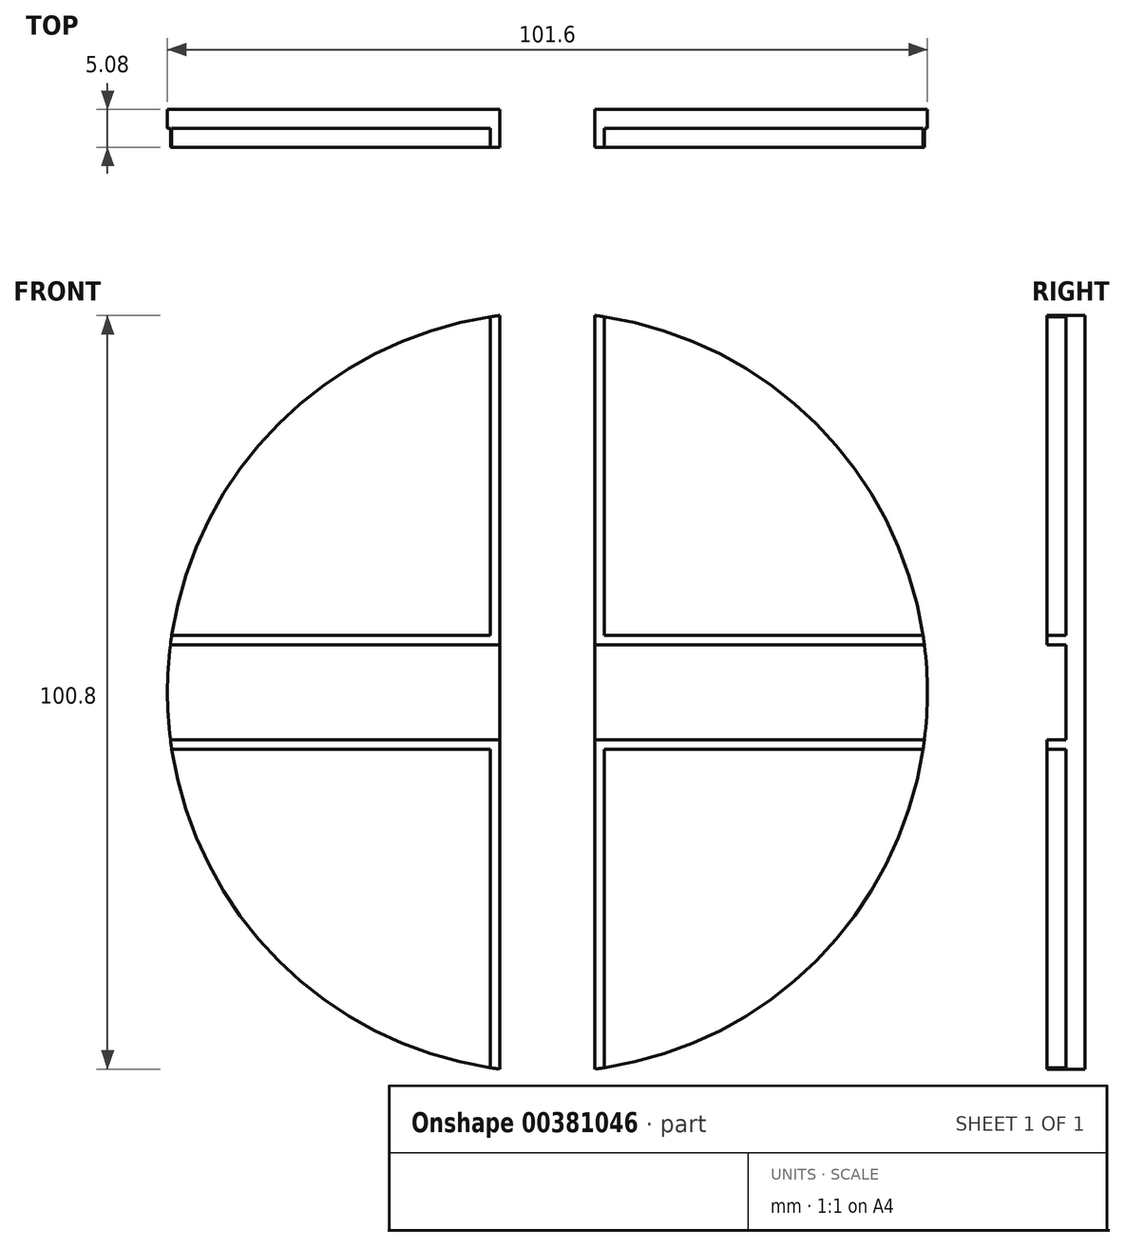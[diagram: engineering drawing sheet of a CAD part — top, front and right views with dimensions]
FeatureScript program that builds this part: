
annotation { "Feature Type Name" : "Feature", "Feature Type Description" : "" }
export const myFeature = defineFeature(function(context is Context, id is Id, definition is map)
    precondition{}
    {
        {
            var Q0;
            Q0=qCreatedBy(makeId("Front.planeOp"),FACE);
            var sketch = newSketch(context, id + "F0", { "sketchPlane" : qUnion([Q0])});
            skCircle(sketch, "E0", {"center": v(0, 0) * mm, "radius": 50.8 * mm});
            skLineSegment(sketch, "E1.bottom", {"start": v(6.35, 6.35) * mm, "end": v(-6.35, 6.35) * mm});
            skLineSegment(sketch, "E1.top", {"start": v(6.35, -6.35) * mm, "end": v(-6.35, -6.35) * mm});
            skLineSegment(sketch, "E1.left", {"start": v(6.35, 6.35) * mm, "end": v(6.35, -6.35) * mm});
            skLineSegment(sketch, "E1.right", {"start": v(-6.35, 6.35) * mm, "end": v(-6.35, -6.35) * mm});
            skLineSegment(sketch, "E2", {"start": v(-6.35, -50.4) * mm, "end": v(-6.35, 50.4) * mm});
            skLineSegment(sketch, "E3", {"start": v(6.35, 50.4) * mm, "end": v(6.35, -50.4) * mm});
            skLineSegment(sketch, "E4", {"start": v(50.4, -6.35) * mm, "end": v(-50.4, -6.35) * mm});
            skPoint(sketch, "E4.startSnap0", {"position": v(0, -6.35) * mm});
            skLineSegment(sketch, "E5", {"start": v(-50.4, 6.35) * mm, "end": v(50.4, 6.35) * mm});
            skPoint(sketch, "E5.startSnap0", {"position": v(0, 6.35) * mm});
            skLineSegment(sketch, "E6", {"start": v(-7.62, 50.23) * mm, "end": v(-7.62, 7.62) * mm});
            skLineSegment(sketch, "E7", {"start": v(-7.62, 7.62) * mm, "end": v(-50.23, 7.62) * mm});
            skLineSegment(sketch, "E8", {"start": v(50.23, 7.62) * mm, "end": v(7.62, 7.62) * mm});
            skLineSegment(sketch, "E9", {"start": v(7.62, 7.62) * mm, "end": v(7.62, 50.23) * mm});
            skLineSegment(sketch, "E10", {"start": v(-7.62, -7.62) * mm, "end": v(-7.62, -50.23) * mm});
            skLineSegment(sketch, "E11", {"start": v(-7.62, -7.62) * mm, "end": v(-50.23, -7.62) * mm});
            skLineSegment(sketch, "E12", {"start": v(7.62, -7.62) * mm, "end": v(50.23, -7.62) * mm});
            skLineSegment(sketch, "E13", {"start": v(7.62, -7.62) * mm, "end": v(7.62, -50.23) * mm});
            skSolve(sketch);
        }
        {
            var Q0;
            {var subQ0=sQuery(id+"F0.wireOp",EDGE,"E4");var subQ1=sQuery(id+"F0.wireOp",EDGE,"E0");var subQ2=makeQuery(id+"F0.imprint","INTERSECT",VERTEX,{"disambiguationData":[OD(1.0)],"derivedFrom":[subQ1,subQ0]});Q0=makeQuery(id+"F0.imprint","IMPRINT",FACE,{"disambiguationData":[TD([[makeQuery(id+"F0.imprint","IMPRINT",EDGE,{"disambiguationData":[TD([[subQ2,1.0]])],"derivedFrom":subQ1}),1.0]])]});}
            var Q1;
            {var subQ0=sQuery(id+"F0.wireOp",EDGE,"E4");var subQ1=sQuery(id+"F0.wireOp",EDGE,"E2");var subQ2=makeQuery(id+"F0.imprint","INTERSECT",VERTEX,{"derivedFrom":[subQ1,subQ0]});Q1=makeQuery(id+"F0.imprint","IMPRINT",FACE,{"disambiguationData":[TD([[makeQuery(id+"F0.imprint","IMPRINT",EDGE,{"disambiguationData":[TD([[subQ2,-1.0]])],"derivedFrom":subQ1}),-1.0]])]});}
            var Q2;
            {var subQ0=sQuery(id+"F0.wireOp",EDGE,"E2");var subQ1=sQuery(id+"F0.wireOp",EDGE,"E0");var subQ2=makeQuery(id+"F0.imprint","INTERSECT",VERTEX,{"disambiguationData":[OD(1.0)],"derivedFrom":[subQ1,subQ0]});Q2=makeQuery(id+"F0.imprint","IMPRINT",FACE,{"disambiguationData":[TD([[makeQuery(id+"F0.imprint","IMPRINT",EDGE,{"disambiguationData":[TD([[subQ2,1.0]])],"derivedFrom":subQ1}),1.0]])]});}
            var Q3;
            {var subQ0=sQuery(id+"F0.wireOp",EDGE,"E4");var subQ1=sQuery(id+"F0.wireOp",EDGE,"E0");var subQ2=makeQuery(id+"F0.imprint","INTERSECT",VERTEX,{"disambiguationData":[OD(0.0)],"derivedFrom":[subQ1,subQ0]});Q3=makeQuery(id+"F0.imprint","IMPRINT",FACE,{"disambiguationData":[TD([[makeQuery(id+"F0.imprint","IMPRINT",EDGE,{"disambiguationData":[TD([[subQ2,-1.0]])],"derivedFrom":subQ1}),1.0]])]});}
            var Q4;
            {var subQ0=sQuery(id+"F0.wireOp",EDGE,"E2");var subQ1=sQuery(id+"F0.wireOp",EDGE,"E0");var subQ2=makeQuery(id+"F0.imprint","INTERSECT",VERTEX,{"disambiguationData":[OD(0.0)],"derivedFrom":[subQ1,subQ0]});Q4=makeQuery(id+"F0.imprint","IMPRINT",FACE,{"disambiguationData":[TD([[makeQuery(id+"F0.imprint","IMPRINT",EDGE,{"disambiguationData":[TD([[subQ2,-1.0]])],"derivedFrom":subQ1}),1.0]])]});}
            var Q5;
            {var subQ0=sQuery(id+"F0.wireOp",EDGE,"E6");Q5=makeQuery(id+"F0.imprint","IMPRINT",FACE,{"disambiguationData":[TD([[makeQuery(id+"F0.imprint","IMPRINT",EDGE,{"derivedFrom":subQ0}),-1.0]])]});}
            var Q6;
            {var subQ0=sQuery(id+"F0.wireOp",EDGE,"E10");Q6=makeQuery(id+"F0.imprint","IMPRINT",FACE,{"disambiguationData":[TD([[makeQuery(id+"F0.imprint","IMPRINT",EDGE,{"derivedFrom":subQ0}),-1.0]])]});}
            var Q7;
            {var subQ0=sQuery(id+"F0.wireOp",EDGE,"E12");Q7=makeQuery(id+"F0.imprint","IMPRINT",FACE,{"disambiguationData":[TD([[makeQuery(id+"F0.imprint","IMPRINT",EDGE,{"derivedFrom":subQ0}),-1.0]])]});}
            var Q8;
            {var subQ7=sQuery(id+"F0.wireOp",EDGE,"E6");Q8=makeQuery(id+"F0.imprint","IMPRINT",FACE,{"disambiguationData":[TD([[makeQuery(id+"F0.imprint","IMPRINT",EDGE,{"derivedFrom":subQ7}),1.0]])]});}
            var Q9;
            {var subQ6=sQuery(id+"F0.wireOp",EDGE,"E10");Q9=makeQuery(id+"F0.imprint","IMPRINT",FACE,{"disambiguationData":[TD([[makeQuery(id+"F0.imprint","IMPRINT",EDGE,{"derivedFrom":subQ6}),1.0]])]});}
            var Q10;
            {var subQ6=sQuery(id+"F0.wireOp",EDGE,"E12");Q10=makeQuery(id+"F0.imprint","IMPRINT",FACE,{"disambiguationData":[TD([[makeQuery(id+"F0.imprint","IMPRINT",EDGE,{"derivedFrom":subQ6}),1.0]])]});}
            var Q11;
            {var subQ0=sQuery(id+"F0.wireOp",EDGE,"E8");Q11=makeQuery(id+"F0.imprint","IMPRINT",FACE,{"disambiguationData":[TD([[makeQuery(id+"F0.imprint","IMPRINT",EDGE,{"derivedFrom":subQ0}),-1.0]])]});}
            var Q12;
            {var subQ5=sQuery(id+"F0.wireOp",EDGE,"E8");Q12=makeQuery(id+"F0.imprint","IMPRINT",FACE,{"disambiguationData":[TD([[makeQuery(id+"F0.imprint","IMPRINT",EDGE,{"derivedFrom":subQ5}),1.0]])]});}
            extrude(context, id + "F1", {"entities" : qUnion([Q0, Q1, Q2, Q3, Q4, Q5, Q6, Q7, Q8, Q9, Q10, Q11, Q12]), "depth" : 2.54 * mm});
        }
        {
            var Q0;
            {var subQ7=sQuery(id+"F0.wireOp",EDGE,"E6");Q0=makeQuery(id+"F0.imprint","IMPRINT",FACE,{"disambiguationData":[TD([[makeQuery(id+"F0.imprint","IMPRINT",EDGE,{"derivedFrom":subQ7}),1.0]])]});}
            var Q1;
            {var subQ5=sQuery(id+"F0.wireOp",EDGE,"E8");Q1=makeQuery(id+"F0.imprint","IMPRINT",FACE,{"disambiguationData":[TD([[makeQuery(id+"F0.imprint","IMPRINT",EDGE,{"derivedFrom":subQ5}),1.0]])]});}
            var Q2;
            {var subQ6=sQuery(id+"F0.wireOp",EDGE,"E12");Q2=makeQuery(id+"F0.imprint","IMPRINT",FACE,{"disambiguationData":[TD([[makeQuery(id+"F0.imprint","IMPRINT",EDGE,{"derivedFrom":subQ6}),1.0]])]});}
            var Q3;
            {var subQ6=sQuery(id+"F0.wireOp",EDGE,"E10");Q3=makeQuery(id+"F0.imprint","IMPRINT",FACE,{"disambiguationData":[TD([[makeQuery(id+"F0.imprint","IMPRINT",EDGE,{"derivedFrom":subQ6}),1.0]])]});}
            extrude(context, id + "F2", {"entities" : qUnion([Q0, Q1, Q2, Q3]), "operationType" : NewBodyOperationType.ADD, "depth" : 5.08 * mm});
        }
    });
